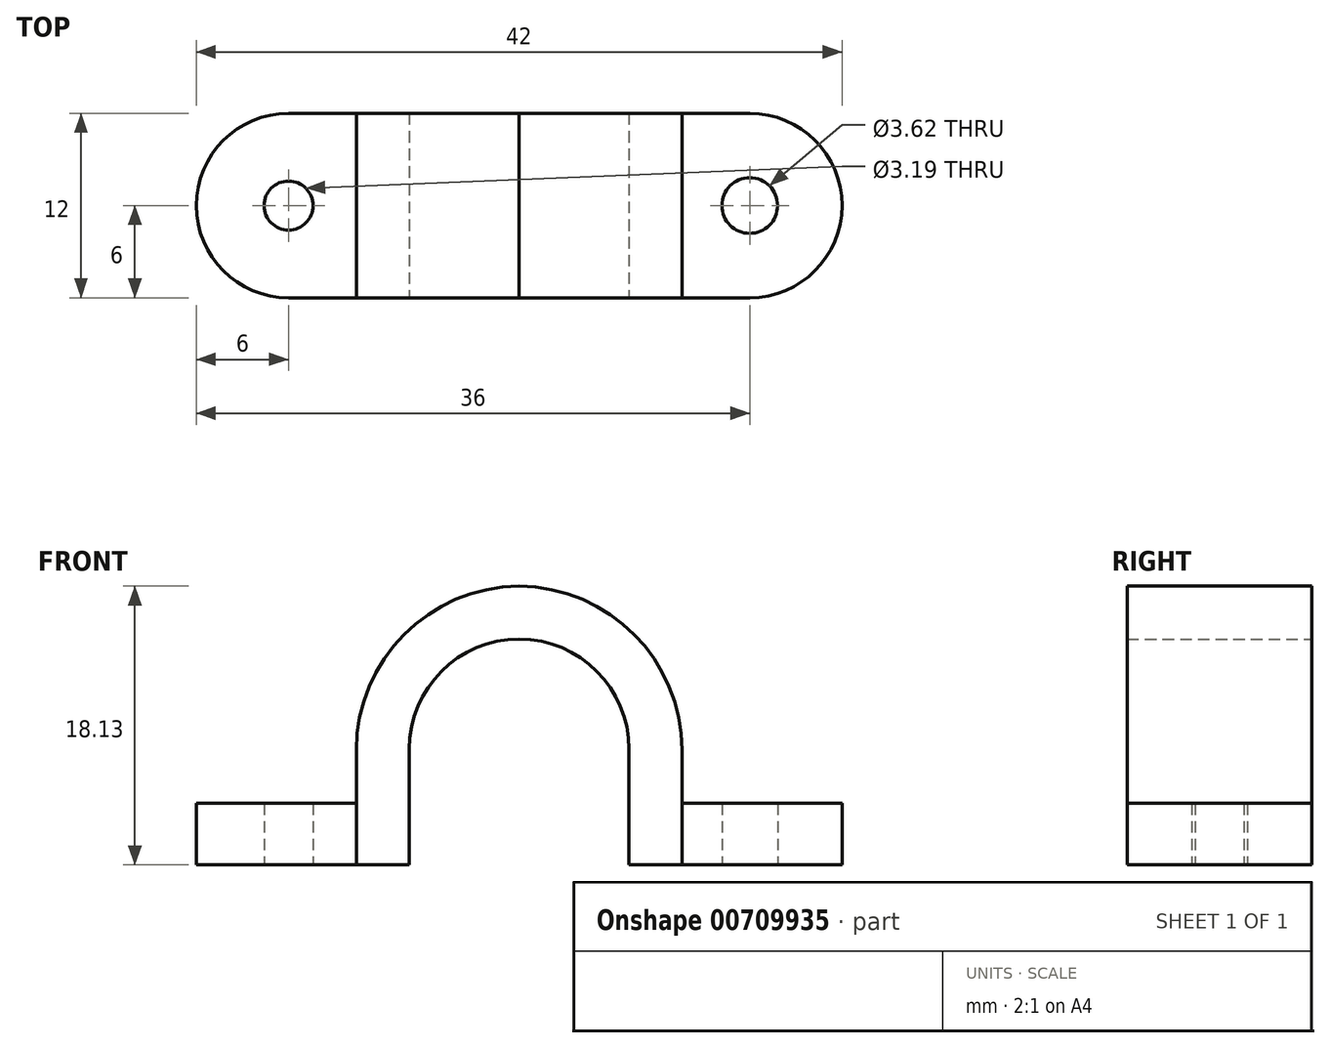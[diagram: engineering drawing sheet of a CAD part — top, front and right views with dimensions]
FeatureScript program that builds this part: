
annotation { "Feature Type Name" : "Feature", "Feature Type Description" : "" }
export const myFeature = defineFeature(function(context is Context, id is Id, definition is map)
    precondition{}
    {
        {
            var Q0;
            Q0=qCreatedBy(makeId("Top.planeOp"),FACE);
            var sketch = newSketch(context, id + "F0", { "sketchPlane" : qUnion([Q0])});
            skLineSegment(sketch, "E0.bottom", {"start": v(6, 0) * mm, "end": v(36, 0) * mm});
            skLineSegment(sketch, "E0.top", {"start": v(6, 12) * mm, "end": v(36, 12) * mm});
            skLineSegment(sketch, "E0.left", {"start": v(0, 6) * mm, "end": v(0, 6) * mm});
            skLineSegment(sketch, "E0.right", {"start": v(42, 6) * mm, "end": v(42, 6) * mm});
            skCircle(sketch, "E1", {"center": v(6, 6) * mm, "radius": 1.6 * mm});
            skPoint(sketch, "E2.visualSharp", {"position": v(0, 12) * mm});
            skArc(sketch, "E2.filletArc", {"start": v(6, 12) * mm, "mid": v(1.76, 10.24) * mm, "end": v(0, 6) * mm});
            skPoint(sketch, "E3.visualSharp", {"position": v(0, 0) * mm});
            skArc(sketch, "E3.filletArc", {"start": v(0, 6) * mm, "mid": v(1.76, 1.76) * mm, "end": v(6, 0) * mm});
            skCircle(sketch, "E4", {"center": v(36, 6) * mm, "radius": 1.81 * mm});
            skPoint(sketch, "E5.visualSharp", {"position": v(42, 12) * mm});
            skArc(sketch, "E5.filletArc", {"start": v(42, 6) * mm, "mid": v(40.24, 10.24) * mm, "end": v(36, 12) * mm});
            skPoint(sketch, "E6.visualSharp", {"position": v(42, 0) * mm});
            skArc(sketch, "E6.filletArc", {"start": v(36, 0) * mm, "mid": v(40.24, 1.76) * mm, "end": v(42, 6) * mm});
            skLineSegment(sketch, "E7", {"start": v(12, 12) * mm, "end": v(12, 0) * mm});
            skLineSegment(sketch, "E8", {"start": v(30, 12) * mm, "end": v(30, 0) * mm});
            skLineSegment(sketch, "E9", {"start": v(10.41, 12) * mm, "end": v(10.41, 0) * mm});
            skLineSegment(sketch, "E10", {"start": v(31.59, 12) * mm, "end": v(31.59, 0) * mm});
            skSolve(sketch);
        }
        {
            var Q0;
            Q0=makeQuery(id+"F0.imprint","IMPRINT",FACE,{"disambiguationData":[TD([[makeQuery(id+"F0.imprint","IMPRINT",EDGE,{"derivedFrom":sQuery(id+"F0.wireOp",EDGE,"E1")}),-1.0]])]});
            var Q1;
            Q1=makeQuery(id+"F0.imprint","IMPRINT",FACE,{"disambiguationData":[TD([[makeQuery(id+"F0.imprint","IMPRINT",EDGE,{"derivedFrom":sQuery(id+"F0.wireOp",EDGE,"E4")}),-1.0]])]});
            extrude(context, id + "F1", {"entities" : qUnion([Q0, Q1]), "depth" : 4 * mm, "offsetDistance" : 25 * mm});
        }
        {
            var Q0;
            {var subQ0=sQuery(id+"F0.wireOp",EDGE,"E7");Q0=makeQuery(id+"F0.imprint","IMPRINT",FACE,{"disambiguationData":[TD([[makeQuery(id+"F0.imprint","IMPRINT",EDGE,{"derivedFrom":subQ0}),1.0]])]});}
            var Q1;
            {var subQ0=sQuery(id+"F0.wireOp",EDGE,"E7");Q1=makeQuery(id+"F0.imprint","IMPRINT",FACE,{"disambiguationData":[TD([[makeQuery(id+"F0.imprint","IMPRINT",EDGE,{"derivedFrom":subQ0}),-1.0]])]});}
            var Q2;
            {var subQ0=sQuery(id+"F0.wireOp",EDGE,"E8");Q2=makeQuery(id+"F0.imprint","IMPRINT",FACE,{"disambiguationData":[TD([[makeQuery(id+"F0.imprint","IMPRINT",EDGE,{"derivedFrom":subQ0}),1.0]])]});}
            extrude(context, id + "F2", {"entities" : qUnion([Q0, Q1, Q2]), "depth" : 18.13 * mm, "offsetDistance" : 25 * mm});
        }
        {
            var Q0;
            Q0=makeQuery(id+"F2.opExtrude","SWEPT_FACE",FACE,{"disambiguationData":[OSD([sQuery(id+"F0.wireOp",EDGE,"E0.top")])]});
            var sketch = newSketch(context, id + "F3", { "sketchPlane" : qUnion([Q0])});
            skCircle(sketch, "E11", {"center": v(-21, 7.54) * mm, "radius": 7.14 * mm});
            skSolve(sketch);
        }
        {
            var Q0;
            Q0=makeQuery(id+"F3.imprint","IMPRINT",FACE,{"disambiguationData":[TD([[makeQuery(id+"F3.imprint","IMPRINT",EDGE,{"derivedFrom":sQuery(id+"F3.wireOp",EDGE,"E11")}),1.0]])]});
            extrude(context, id + "F4", {"entities" : qUnion([Q0]), "operationType" : NewBodyOperationType.REMOVE, "oppositeDirection" : true, "depth" : 25.4 * mm, "offsetDistance" : 25.4 * mm});
        }
        {
            var Q0;
            {var subQ0=sQuery(id+"F0.wireOp",EDGE,"E7");Q0=makeQuery(id+"F0.imprint","IMPRINT",FACE,{"disambiguationData":[TD([[makeQuery(id+"F0.imprint","IMPRINT",EDGE,{"derivedFrom":subQ0}),1.0]])]});}
            var sketch = newSketch(context, id + "F5", { "sketchPlane" : qUnion([Q0])});
            skLineSegment(sketch, "E12.bottom", {"start": v(28.14, 12) * mm, "end": v(13.86, 12) * mm});
            skLineSegment(sketch, "E12.top", {"start": v(28.14, 0) * mm, "end": v(13.86, 0) * mm});
            skLineSegment(sketch, "E12.left", {"start": v(28.14, 12) * mm, "end": v(28.14, 0) * mm});
            skLineSegment(sketch, "E12.right", {"start": v(13.86, 12) * mm, "end": v(13.86, 0) * mm});
            skSolve(sketch);
        }
        {
            var Q0;
            Q0=makeQuery(id+"F5.imprint","IMPRINT",FACE,{"disambiguationData":[TD([[makeQuery(id+"F5.imprint","IMPRINT",EDGE,{"derivedFrom":sQuery(id+"F5.wireOp",EDGE,"E12.bottom")}),-1.0]])]});
            extrude(context, id + "F6", {"entities" : qUnion([Q0]), "operationType" : NewBodyOperationType.REMOVE, "depth" : 7.54 * mm, "offsetDistance" : 25.4 * mm});
        }
        {
            var Q0;
            Q0=makeQuery(id+"F2.opExtrude","CAP_EDGE",EDGE,{"disambiguationData":[OSD([sQuery(id+"F0.wireOp",EDGE,"E9")])],"isStart":false});
            var Q1;
            Q1=makeQuery(id+"F2.opExtrude","CAP_EDGE",EDGE,{"disambiguationData":[OSD([sQuery(id+"F0.wireOp",EDGE,"E10")])],"isStart":false});
            fillet(context, id + "F7", {"entities" : qUnion([Q0, Q1]), "radius" : 10.67 * mm, "tangentPropagation" : true, "allowEdgeOverflow" : false});
        }
    });
